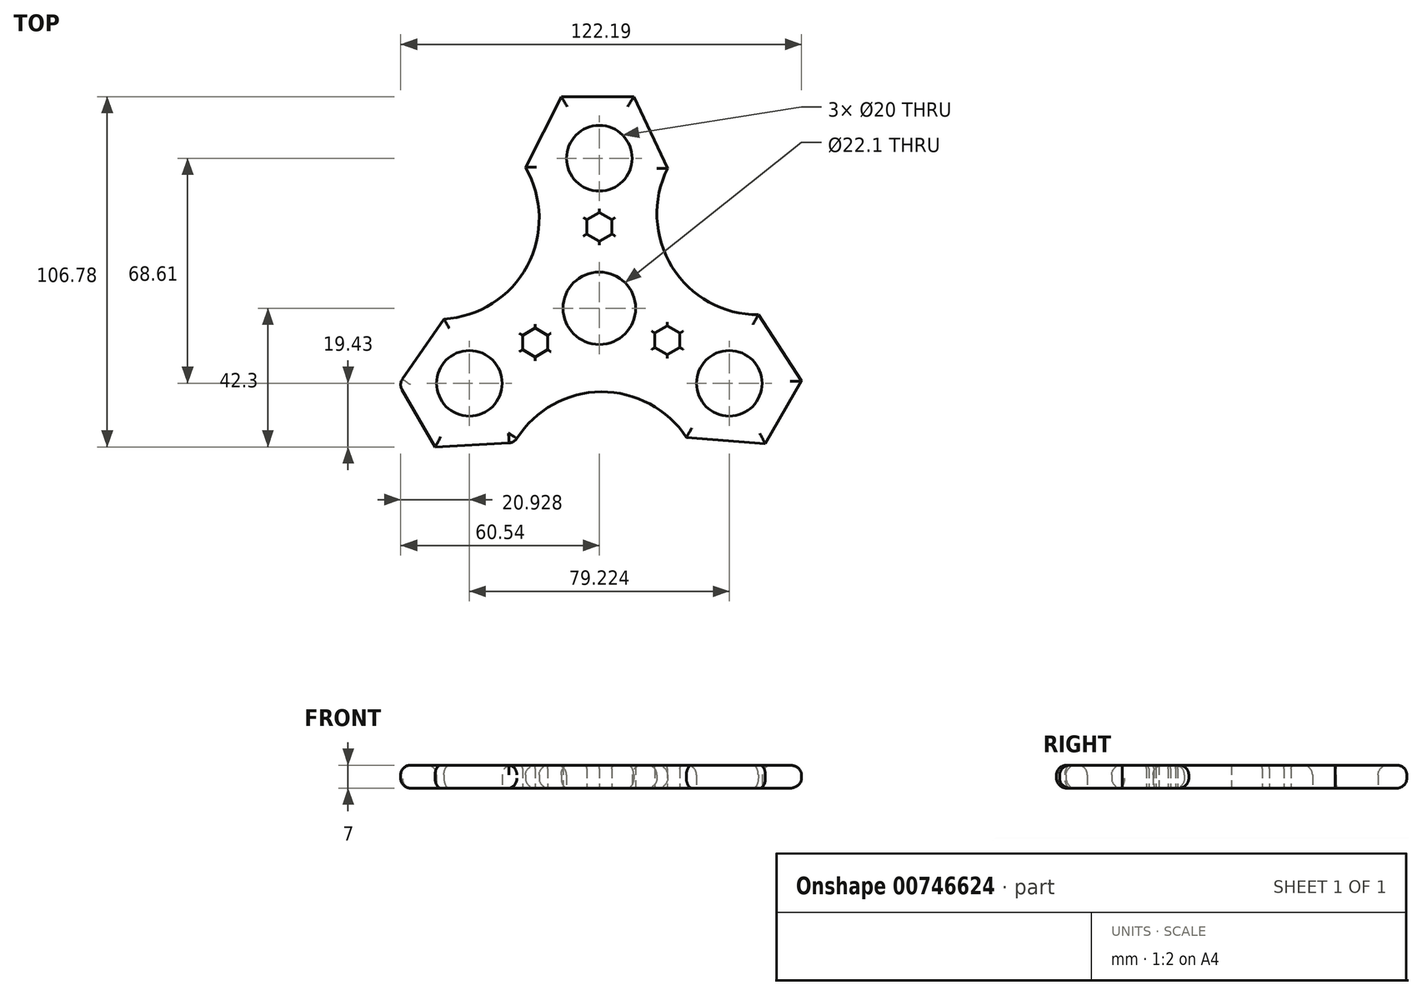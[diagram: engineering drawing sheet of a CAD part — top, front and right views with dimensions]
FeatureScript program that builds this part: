
annotation { "Feature Type Name" : "Feature", "Feature Type Description" : "" }
export const myFeature = defineFeature(function(context is Context, id is Id, definition is map)
    precondition{}
    {
        {
            var Q0;
            Q0=qCreatedBy(makeId("Top.planeOp"),FACE);
            var sketch = newSketch(context, id + "F0", { "sketchPlane" : qUnion([Q0])});
            skCircle(sketch, "E0", {"center": v(0, 0) * mm, "radius": 11.05 * mm});
            skCircle(sketch, "E1", {"center": v(0, 45.74) * mm, "radius": 10 * mm});
            skCircle(sketch, "E2.1.0", {"center": v(-39.61, -22.87) * mm, "radius": 10 * mm});
            skCircle(sketch, "E2.2.0", {"center": v(39.61, -22.87) * mm, "radius": 10 * mm});
            skLineSegment(sketch, "E3", {"start": v(0, 64.48) * mm, "end": v(-11.6, 64.48) * mm});
            skLineSegment(sketch, "E4", {"start": v(-11.6, 64.48) * mm, "end": v(10.5, 64.48) * mm});
            skLineSegment(sketch, "E5.1.0", {"start": v(-50.04, -42.3) * mm, "end": v(-61.09, -23.16) * mm});
            skLineSegment(sketch, "E5.2.0", {"start": v(61.65, -22.19) * mm, "end": v(50.6, -41.33) * mm});
            skLineSegment(sketch, "E6", {"start": v(-11.6, 64.48) * mm, "end": v(-22.52, 42.94) * mm});
            skLineSegment(sketch, "E7.1.0", {"start": v(-50.04, -42.3) * mm, "end": v(-25.93, -40.97) * mm});
            skLineSegment(sketch, "E7.2.0", {"start": v(61.65, -22.19) * mm, "end": v(48.45, -1.97) * mm});
            skLineSegment(sketch, "E8", {"start": v(10.5, 64.48) * mm, "end": v(20.84, 42.66) * mm});
            skLineSegment(sketch, "E9.1.0", {"start": v(-61.09, -23.16) * mm, "end": v(-47.37, -3.28) * mm});
            skLineSegment(sketch, "E9.2.0", {"start": v(50.6, -41.33) * mm, "end": v(26.53, -39.38) * mm});
            skArc(sketch, "E10", {"start": v(-47.37, -3.28) * mm, "mid": v(-22, 12.88) * mm, "end": v(-22.52, 42.94) * mm});
            skArc(sketch, "E11.1.0", {"start": v(26.53, -39.38) * mm, "mid": v(-0.15, -25.5) * mm, "end": v(-25.93, -40.97) * mm});
            skArc(sketch, "E11.2.0", {"start": v(20.84, 42.66) * mm, "mid": v(22.15, 12.62) * mm, "end": v(48.45, -1.97) * mm});
            skCircle(sketch, "E12.cCircle", {"center": v(0, 24.84) * mm, "radius": 3.8 * mm, "construction": true});
            skLineSegment(sketch, "E12.0", {"start": v(3.8, 27.03) * mm, "end": v(3.8, 22.64) * mm});
            skLineSegment(sketch, "E12.1", {"start": v(3.8, 22.64) * mm, "end": v(0, 20.44) * mm});
            skLineSegment(sketch, "E12.2", {"start": v(0, 20.44) * mm, "end": v(-3.8, 22.64) * mm});
            skLineSegment(sketch, "E12.3", {"start": v(-3.8, 22.64) * mm, "end": v(-3.8, 27.03) * mm});
            skLineSegment(sketch, "E12.4", {"start": v(-3.8, 27.03) * mm, "end": v(0, 29.23) * mm});
            skLineSegment(sketch, "E12.5", {"start": v(0, 29.23) * mm, "end": v(3.8, 27.03) * mm});
            skPoint(sketch, "E12.0.midPoint", {"position": v(3.8, 24.84) * mm});
            skCircle(sketch, "E13.1.0", {"center": v(-19.6, -10.44) * mm, "radius": 3.8 * mm, "construction": true});
            skLineSegment(sketch, "E13.1.1", {"start": v(-23.4, -12.64) * mm, "end": v(-23.4, -8.24) * mm});
            skLineSegment(sketch, "E13.1.2", {"start": v(-23.4, -8.24) * mm, "end": v(-19.6, -6.04) * mm});
            skLineSegment(sketch, "E13.1.3", {"start": v(-19.6, -6.04) * mm, "end": v(-15.79, -8.24) * mm});
            skLineSegment(sketch, "E13.1.4", {"start": v(-15.79, -8.24) * mm, "end": v(-15.79, -12.64) * mm});
            skLineSegment(sketch, "E13.1.5", {"start": v(-15.79, -12.64) * mm, "end": v(-19.6, -14.84) * mm});
            skLineSegment(sketch, "E13.1.6", {"start": v(-19.6, -14.84) * mm, "end": v(-23.4, -12.64) * mm});
            skCircle(sketch, "E13.2.0", {"center": v(20.75, -9.77) * mm, "radius": 3.8 * mm, "construction": true});
            skLineSegment(sketch, "E13.2.1", {"start": v(24.56, -11.97) * mm, "end": v(20.75, -14.17) * mm});
            skLineSegment(sketch, "E13.2.2", {"start": v(20.75, -14.17) * mm, "end": v(16.95, -11.97) * mm});
            skLineSegment(sketch, "E13.2.3", {"start": v(16.95, -11.97) * mm, "end": v(16.95, -7.57) * mm});
            skLineSegment(sketch, "E13.2.4", {"start": v(16.95, -7.57) * mm, "end": v(20.75, -5.37) * mm});
            skLineSegment(sketch, "E13.2.5", {"start": v(20.75, -5.37) * mm, "end": v(24.56, -7.57) * mm});
            skLineSegment(sketch, "E13.2.6", {"start": v(24.56, -7.57) * mm, "end": v(24.56, -11.97) * mm});
            skPoint(sketch, "E13.center", {"position": v(0.39, 1.54) * mm});
            skSolve(sketch);
        }
        {
            var Q0;
            Q0 = qSketchRegion(id + "F0", true);
            extrude(context, id + "F1", {"entities" : qUnion([Q0]), "depth" : 7 * mm, "offsetDistance" : 25.4 * mm});
        }
        {
            var Q0;
            Q0=makeQuery(id+"F1.opExtrude","CAP_EDGE",EDGE,{"disambiguationData":[OSD([sQuery(id+"F0.wireOp",EDGE,"E10")])],"isStart":false});
            var Q1;
            Q1=makeQuery(id+"F1.opExtrude","CAP_EDGE",EDGE,{"disambiguationData":[OSD([sQuery(id+"F0.wireOp",EDGE,"E9.1.0")])],"isStart":false});
            var Q2;
            Q2=makeQuery(id+"F1.opExtrude","CAP_EDGE",EDGE,{"disambiguationData":[OSD([sQuery(id+"F0.wireOp",EDGE,"E5.1.0")])],"isStart":false});
            var Q3;
            Q3=makeQuery(id+"F1.opExtrude","CAP_EDGE",EDGE,{"disambiguationData":[OSD([sQuery(id+"F0.wireOp",EDGE,"E7.1.0")])],"isStart":false});
            var Q4;
            Q4=makeQuery(id+"F1.opExtrude","CAP_EDGE",EDGE,{"disambiguationData":[OSD([sQuery(id+"F0.wireOp",EDGE,"E11.1.0")])],"isStart":false});
            var Q5;
            Q5=makeQuery(id+"F1.opExtrude","CAP_EDGE",EDGE,{"disambiguationData":[OSD([sQuery(id+"F0.wireOp",EDGE,"E9.2.0")])],"isStart":false});
            var Q6;
            Q6=makeQuery(id+"F1.opExtrude","CAP_EDGE",EDGE,{"disambiguationData":[OSD([sQuery(id+"F0.wireOp",EDGE,"E5.2.0")])],"isStart":false});
            var Q7;
            Q7=makeQuery(id+"F1.opExtrude","CAP_EDGE",EDGE,{"disambiguationData":[OSD([sQuery(id+"F0.wireOp",EDGE,"E7.2.0")])],"isStart":false});
            var Q8;
            Q8=makeQuery(id+"F1.opExtrude","CAP_EDGE",EDGE,{"disambiguationData":[OSD([sQuery(id+"F0.wireOp",EDGE,"E11.2.0")])],"isStart":false});
            var Q9;
            Q9=makeQuery(id+"F1.opExtrude","CAP_EDGE",EDGE,{"disambiguationData":[OSD([sQuery(id+"F0.wireOp",EDGE,"E8")])],"isStart":false});
            var Q10;
            Q10=makeQuery(id+"F1.opExtrude","CAP_EDGE",EDGE,{"disambiguationData":[OSD([sQuery(id+"F0.wireOp",EDGE,"E4")])],"isStart":false});
            var Q11;
            Q11=makeQuery(id+"F1.opExtrude","CAP_EDGE",EDGE,{"disambiguationData":[OSD([sQuery(id+"F0.wireOp",EDGE,"E6")])],"isStart":false});
            var Q12;
            Q12=makeQuery(id+"F1.opExtrude","CAP_EDGE",EDGE,{"disambiguationData":[OSD([sQuery(id+"F0.wireOp",EDGE,"E1")])],"isStart":false});
            var Q13;
            Q13=makeQuery(id+"F1.opExtrude","CAP_EDGE",EDGE,{"disambiguationData":[OSD([sQuery(id+"F0.wireOp",EDGE,"E2.1.0")])],"isStart":false});
            var Q14;
            Q14=makeQuery(id+"F1.opExtrude","CAP_EDGE",EDGE,{"disambiguationData":[OSD([sQuery(id+"F0.wireOp",EDGE,"E2.2.0")])],"isStart":false});
            var Q15;
            Q15=makeQuery(id+"F1.opExtrude","CAP_EDGE",EDGE,{"disambiguationData":[OSD([sQuery(id+"F0.wireOp",EDGE,"E11.1.0")])],"isStart":true});
            var Q16;
            Q16=makeQuery(id+"F1.opExtrude","CAP_EDGE",EDGE,{"disambiguationData":[OSD([sQuery(id+"F0.wireOp",EDGE,"E9.2.0")])],"isStart":true});
            var Q17;
            Q17=makeQuery(id+"F1.opExtrude","CAP_EDGE",EDGE,{"disambiguationData":[OSD([sQuery(id+"F0.wireOp",EDGE,"E5.2.0")])],"isStart":true});
            var Q18;
            Q18=makeQuery(id+"F1.opExtrude","CAP_EDGE",EDGE,{"disambiguationData":[OSD([sQuery(id+"F0.wireOp",EDGE,"E7.2.0")])],"isStart":true});
            var Q19;
            Q19=makeQuery(id+"F1.opExtrude","CAP_EDGE",EDGE,{"disambiguationData":[OSD([sQuery(id+"F0.wireOp",EDGE,"E11.2.0")])],"isStart":true});
            var Q20;
            Q20=makeQuery(id+"F1.opExtrude","CAP_EDGE",EDGE,{"disambiguationData":[OSD([sQuery(id+"F0.wireOp",EDGE,"E4")])],"isStart":true});
            var Q21;
            Q21=makeQuery(id+"F1.opExtrude","CAP_EDGE",EDGE,{"disambiguationData":[OSD([sQuery(id+"F0.wireOp",EDGE,"E8")])],"isStart":true});
            var Q22;
            Q22=makeQuery(id+"F1.opExtrude","CAP_EDGE",EDGE,{"disambiguationData":[OSD([sQuery(id+"F0.wireOp",EDGE,"E6")])],"isStart":true});
            var Q23;
            Q23=makeQuery(id+"F1.opExtrude","CAP_EDGE",EDGE,{"disambiguationData":[OSD([sQuery(id+"F0.wireOp",EDGE,"E10")])],"isStart":true});
            var Q24;
            Q24=makeQuery(id+"F1.opExtrude","CAP_EDGE",EDGE,{"disambiguationData":[OSD([sQuery(id+"F0.wireOp",EDGE,"E9.1.0")])],"isStart":true});
            fillet(context, id + "F2", {"entities" : qUnion([Q0, Q1, Q2, Q3, Q4, Q5, Q6, Q7, Q8, Q9, Q10, Q11, Q12, Q13, Q14, Q15, Q16, Q17, Q18, Q19, Q20, Q21, Q22, Q23, Q24]), "radius" : 3 * mm, "tangentPropagation" : true, "defaultsChanged" : false, "vertexSettings" : [], "allowEdgeOverflow" : false});
        }
        {
            var Q0;
            Q0=makeQuery(id+"F1.opExtrude","CAP_EDGE",EDGE,{"disambiguationData":[OSD([sQuery(id+"F0.wireOp",EDGE,"E7.1.0")])],"isStart":true});
            var Q1;
            Q1=makeQuery(id+"F1.opExtrude","CAP_EDGE",EDGE,{"disambiguationData":[OSD([sQuery(id+"F0.wireOp",EDGE,"E5.1.0")])],"isStart":true});
            fillet(context, id + "F3", {"entities" : qUnion([Q0, Q1]), "radius" : 3 * mm, "tangentPropagation" : true, "allowEdgeOverflow" : false});
        }
        {
            var Q0;
            Q0=makeQuery(id+"F1.opExtrude","CAP_EDGE",EDGE,{"disambiguationData":[OSD([sQuery(id+"F0.wireOp",EDGE,"E12.1")])],"isStart":false});
            var Q1;
            Q1=makeQuery(id+"F1.opExtrude","CAP_EDGE",EDGE,{"disambiguationData":[OSD([sQuery(id+"F0.wireOp",EDGE,"E12.0")])],"isStart":false});
            var Q2;
            Q2=makeQuery(id+"F1.opExtrude","CAP_EDGE",EDGE,{"disambiguationData":[OSD([sQuery(id+"F0.wireOp",EDGE,"E12.5")])],"isStart":false});
            var Q3;
            Q3=makeQuery(id+"F1.opExtrude","CAP_EDGE",EDGE,{"disambiguationData":[OSD([sQuery(id+"F0.wireOp",EDGE,"E12.4")])],"isStart":false});
            var Q4;
            Q4=makeQuery(id+"F1.opExtrude","CAP_EDGE",EDGE,{"disambiguationData":[OSD([sQuery(id+"F0.wireOp",EDGE,"E12.2")])],"isStart":false});
            var Q5;
            Q5=makeQuery(id+"F1.opExtrude","CAP_EDGE",EDGE,{"disambiguationData":[OSD([sQuery(id+"F0.wireOp",EDGE,"E12.3")])],"isStart":false});
            var Q6;
            Q6=makeQuery(id+"F1.opExtrude","CAP_EDGE",EDGE,{"disambiguationData":[OSD([sQuery(id+"F0.wireOp",EDGE,"E13.2.4")])],"isStart":false});
            var Q7;
            Q7=makeQuery(id+"F1.opExtrude","CAP_EDGE",EDGE,{"disambiguationData":[OSD([sQuery(id+"F0.wireOp",EDGE,"E13.2.3")])],"isStart":false});
            var Q8;
            Q8=makeQuery(id+"F1.opExtrude","CAP_EDGE",EDGE,{"disambiguationData":[OSD([sQuery(id+"F0.wireOp",EDGE,"E13.2.2")])],"isStart":false});
            var Q9;
            Q9=makeQuery(id+"F1.opExtrude","CAP_EDGE",EDGE,{"disambiguationData":[OSD([sQuery(id+"F0.wireOp",EDGE,"E13.2.1")])],"isStart":false});
            var Q10;
            Q10=makeQuery(id+"F1.opExtrude","CAP_EDGE",EDGE,{"disambiguationData":[OSD([sQuery(id+"F0.wireOp",EDGE,"E13.2.6")])],"isStart":false});
            var Q11;
            Q11=makeQuery(id+"F1.opExtrude","CAP_EDGE",EDGE,{"disambiguationData":[OSD([sQuery(id+"F0.wireOp",EDGE,"E13.2.5")])],"isStart":false});
            var Q12;
            Q12=makeQuery(id+"F1.opExtrude","CAP_EDGE",EDGE,{"disambiguationData":[OSD([sQuery(id+"F0.wireOp",EDGE,"E13.1.5")])],"isStart":false});
            var Q13;
            Q13=makeQuery(id+"F1.opExtrude","CAP_EDGE",EDGE,{"disambiguationData":[OSD([sQuery(id+"F0.wireOp",EDGE,"E13.1.4")])],"isStart":false});
            var Q14;
            Q14=makeQuery(id+"F1.opExtrude","CAP_EDGE",EDGE,{"disambiguationData":[OSD([sQuery(id+"F0.wireOp",EDGE,"E13.1.3")])],"isStart":false});
            var Q15;
            Q15=makeQuery(id+"F1.opExtrude","CAP_EDGE",EDGE,{"disambiguationData":[OSD([sQuery(id+"F0.wireOp",EDGE,"E13.1.2")])],"isStart":false});
            var Q16;
            Q16=makeQuery(id+"F1.opExtrude","CAP_EDGE",EDGE,{"disambiguationData":[OSD([sQuery(id+"F0.wireOp",EDGE,"E13.1.1")])],"isStart":false});
            var Q17;
            Q17=makeQuery(id+"F1.opExtrude","CAP_EDGE",EDGE,{"disambiguationData":[OSD([sQuery(id+"F0.wireOp",EDGE,"E13.1.6")])],"isStart":false});
            fillet(context, id + "F4", {"entities" : qUnion([Q0, Q1, Q2, Q3, Q4, Q5, Q6, Q7, Q8, Q9, Q10, Q11, Q12, Q13, Q14, Q15, Q16, Q17]), "radius" : 1 * mm, "tangentPropagation" : true, "allowEdgeOverflow" : false});
        }
    });
